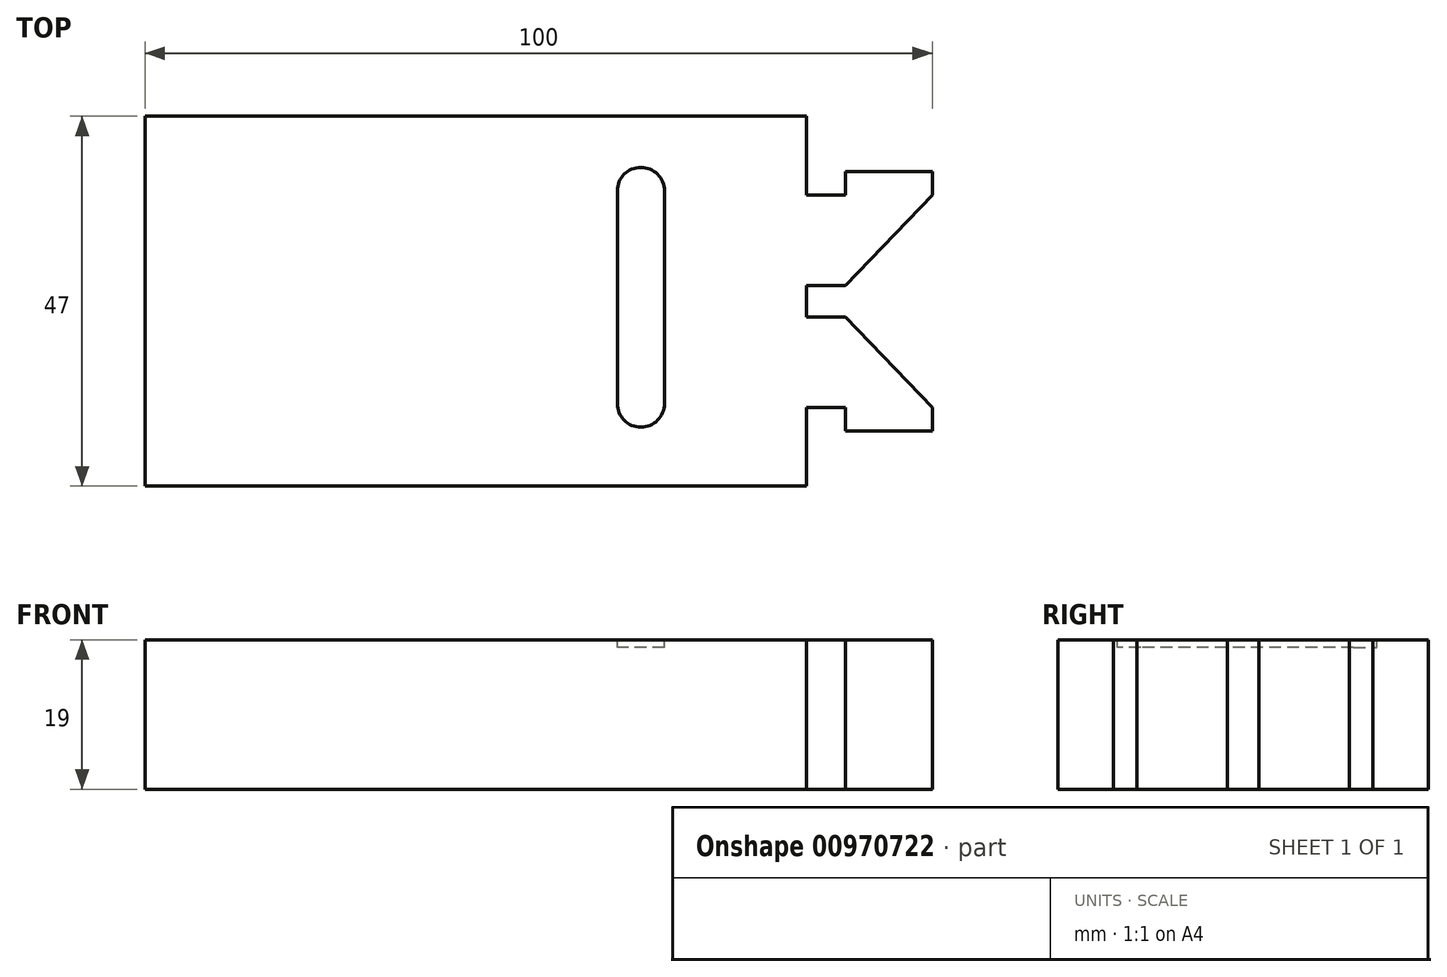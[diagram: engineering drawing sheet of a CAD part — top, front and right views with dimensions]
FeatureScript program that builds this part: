
annotation { "Feature Type Name" : "Feature", "Feature Type Description" : "" }
export const myFeature = defineFeature(function(context is Context, id is Id, definition is map)
    precondition{}
    {
        {
            var Q0;
            Q0=qCreatedBy(makeId("Top.planeOp"),FACE);
            var sketch = newSketch(context, id + "F0", { "sketchPlane" : qUnion([Q0])});
            skLineSegment(sketch, "E0", {"start": v(0, 0) * mm, "end": v(0, 48) * mm});
            skLineSegment(sketch, "E1", {"start": v(0, 48) * mm, "end": v(84, 48) * mm});
            skLineSegment(sketch, "E2", {"start": v(84, 48) * mm, "end": v(84, 38) * mm});
            skLineSegment(sketch, "E3", {"start": v(84, 38) * mm, "end": v(89, 38) * mm});
            skLineSegment(sketch, "E4", {"start": v(89, 38) * mm, "end": v(89, 41) * mm});
            skLineSegment(sketch, "E5", {"start": v(89, 41) * mm, "end": v(100, 41) * mm});
            skLineSegment(sketch, "E6", {"start": v(100, 41) * mm, "end": v(100, 38) * mm});
            skLineSegment(sketch, "E7", {"start": v(84, 26.5) * mm, "end": v(84, 22.5) * mm});
            skLineSegment(sketch, "E8", {"start": v(84, 26.5) * mm, "end": v(89, 26.5) * mm});
            skLineSegment(sketch, "E9", {"start": v(89, 26.5) * mm, "end": v(100, 38) * mm});
            skLineSegment(sketch, "E10", {"start": v(84, 24.5) * mm, "end": v(80.2, 24.5) * mm});
            skLineSegment(sketch, "E11.MirrorCS", {"start": v(84, 22.5) * mm, "end": v(89, 22.5) * mm});
            skLineSegment(sketch, "E12.MirrorCS", {"start": v(89, 22.5) * mm, "end": v(100, 11) * mm});
            skLineSegment(sketch, "E13.MirrorCS", {"start": v(100, 8) * mm, "end": v(100, 11) * mm});
            skLineSegment(sketch, "E14.MirrorCS", {"start": v(89, 8) * mm, "end": v(100, 8) * mm});
            skLineSegment(sketch, "E15.MirrorCS", {"start": v(89, 11) * mm, "end": v(89, 8) * mm});
            skLineSegment(sketch, "E16.MirrorCS", {"start": v(84, 11) * mm, "end": v(89, 11) * mm});
            skLineSegment(sketch, "E17.MirrorCS", {"start": v(84, 1) * mm, "end": v(84, 11) * mm});
            skLineSegment(sketch, "E18.MirrorCS", {"start": v(0, 1) * mm, "end": v(84, 1) * mm});
            skSolve(sketch);
        }
        {
            var Q0;
            {var subQ4=sQuery(id+"F0.wireOp",EDGE,"E1");Q0=makeQuery(id+"F0.imprint","IMPRINT",FACE,{"disambiguationData":[TD([[makeQuery(id+"F0.imprint","IMPRINT",EDGE,{"derivedFrom":subQ4}),-1.0]])]});}
            extrude(context, id + "F1", {"entities" : qUnion([Q0]), "depth" : 19 * mm, "offsetDistance" : 25 * mm});
        }
        {
            var Q0;
            Q0=makeQuery(id+"F1.opExtrude","CAP_FACE",FACE,{"disambiguationData":[OSD([sQuery(id+"F0.wireOp",EDGE,"E0"),sQuery(id+"F0.wireOp",EDGE,"E1"),sQuery(id+"F0.wireOp",EDGE,"E2"),sQuery(id+"F0.wireOp",EDGE,"E3"),sQuery(id+"F0.wireOp",EDGE,"E4"),sQuery(id+"F0.wireOp",EDGE,"E5"),sQuery(id+"F0.wireOp",EDGE,"E6"),sQuery(id+"F0.wireOp",EDGE,"E7"),sQuery(id+"F0.wireOp",EDGE,"E8"),sQuery(id+"F0.wireOp",EDGE,"E9"),sQuery(id+"F0.wireOp",EDGE,"E11.MirrorCS"),sQuery(id+"F0.wireOp",EDGE,"E12.MirrorCS"),sQuery(id+"F0.wireOp",EDGE,"E13.MirrorCS"),sQuery(id+"F0.wireOp",EDGE,"E14.MirrorCS"),sQuery(id+"F0.wireOp",EDGE,"E15.MirrorCS"),sQuery(id+"F0.wireOp",EDGE,"E16.MirrorCS"),sQuery(id+"F0.wireOp",EDGE,"E17.MirrorCS"),sQuery(id+"F0.wireOp",EDGE,"E18.MirrorCS")])],"isStart":false});
            var sketch = newSketch(context, id + "F2", { "sketchPlane" : qUnion([Q0])});
            skLineSegment(sketch, "E19", {"start": v(0, 1) * mm, "end": v(63, 1) * mm});
            skLineSegment(sketch, "E20", {"start": v(60, 38.5) * mm, "end": v(60, 11.5) * mm});
            skArc(sketch, "E21", {"start": v(60, 38.5) * mm, "mid": v(63, 41.5) * mm, "end": v(66, 38.5) * mm});
            skLineSegment(sketch, "E22", {"start": v(66, 38.5) * mm, "end": v(66, 11.5) * mm});
            skArc(sketch, "E23", {"start": v(66, 11.5) * mm, "mid": v(63, 8.5) * mm, "end": v(60, 11.5) * mm});
            skSolve(sketch);
        }
        {
            var Q0;
            Q0 = qSketchRegion(id + "F2", true);
            extrude(context, id + "F3", {"entities" : qUnion([Q0]), "operationType" : NewBodyOperationType.REMOVE, "oppositeDirection" : true, "depth" : 1 * mm, "offsetDistance" : 25 * mm});
        }
    });
